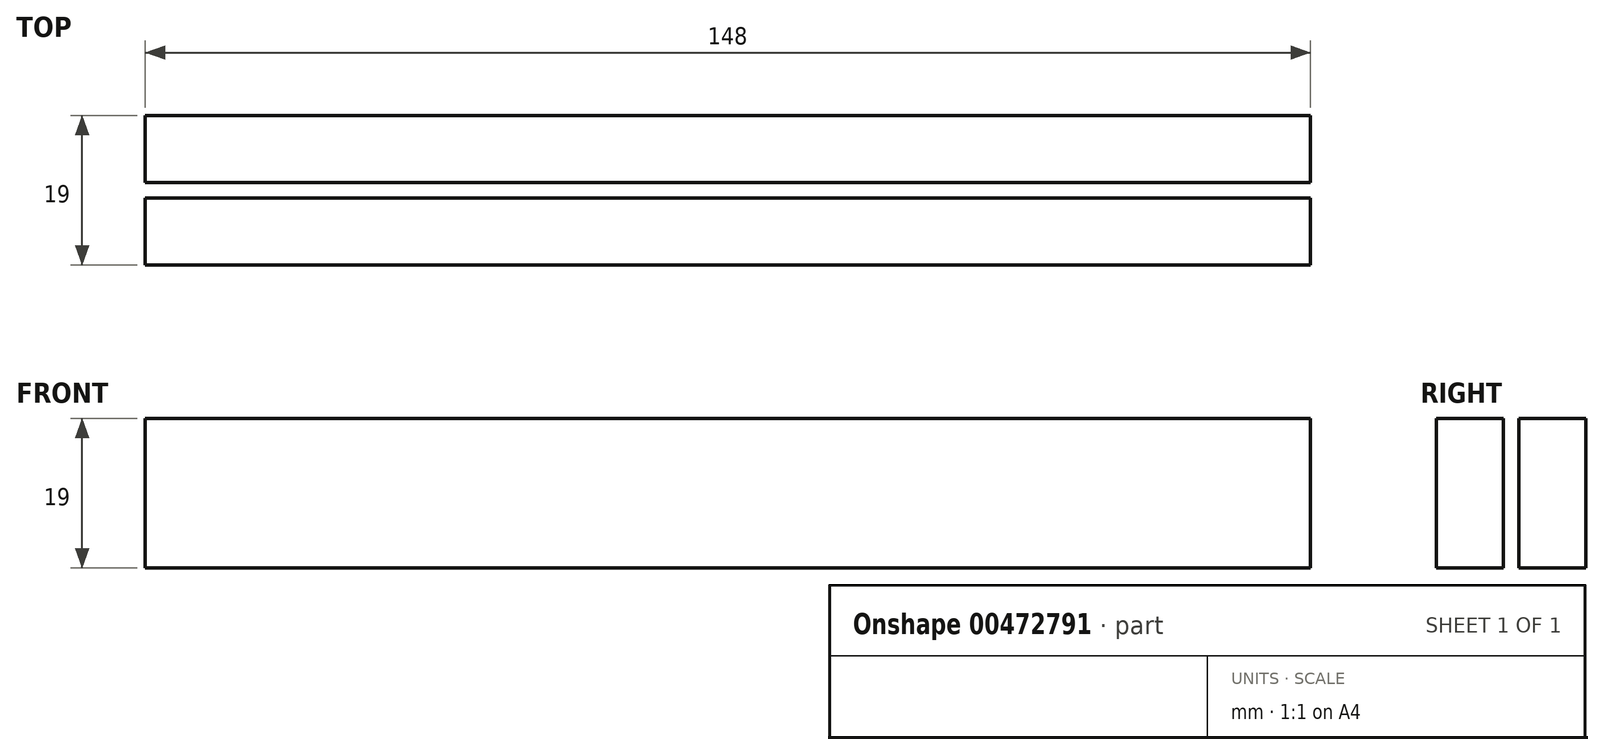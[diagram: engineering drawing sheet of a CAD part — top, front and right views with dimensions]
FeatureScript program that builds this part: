
annotation { "Feature Type Name" : "Feature", "Feature Type Description" : "" }
export const myFeature = defineFeature(function(context is Context, id is Id, definition is map)
    precondition{}
    {
        {
            var Q0;
            Q0=qCreatedBy(makeId("Top.planeOp"),FACE);
            var sketch = newSketch(context, id + "F0", { "sketchPlane" : qUnion([Q0])});
            skLineSegment(sketch, "E0.bottom", {"start": v(74, -9.5) * mm, "end": v(-74, -9.5) * mm});
            skLineSegment(sketch, "E0.top", {"start": v(74, 9.5) * mm, "end": v(-74, 9.5) * mm});
            skLineSegment(sketch, "E0.left", {"start": v(74, -9.5) * mm, "end": v(74, 9.5) * mm});
            skLineSegment(sketch, "E0.right", {"start": v(-74, -9.5) * mm, "end": v(-74, 9.5) * mm});
            skPoint(sketch, "E0.middle", {"position": v(0, 0) * mm});
            skSolve(sketch);
        }
        {
            var Q0;
            Q0=makeQuery(id+"F0.imprint","IMPRINT",FACE,{"disambiguationData":[TD([[makeQuery(id+"F0.imprint","IMPRINT",EDGE,{"derivedFrom":sQuery(id+"F0.wireOp",EDGE,"E0.bottom")}),-1.0]])]});
            extrude(context, id + "F1", {"entities" : qUnion([Q0]), "depth" : 19 * mm});
        }
        {
            var Q0;
            Q0=makeQuery(id+"F1.opExtrude","CAP_FACE",FACE,{"disambiguationData":[OSD([sQuery(id+"F0.wireOp",EDGE,"E0.bottom"),sQuery(id+"F0.wireOp",EDGE,"E0.top"),sQuery(id+"F0.wireOp",EDGE,"E0.left"),sQuery(id+"F0.wireOp",EDGE,"E0.right")])],"isStart":false});
            var sketch = newSketch(context, id + "F2", { "sketchPlane" : qUnion([Q0])});
            skLineSegment(sketch, "E1", {"start": v(-74, 9.5) * mm, "end": v(-74, -9.5) * mm, "construction": true});
            skLineSegment(sketch, "E2", {"start": v(-74, 0) * mm, "end": v(-74, 1) * mm, "construction": true});
            skLineSegment(sketch, "E3.bottom", {"start": v(-74, 1) * mm, "end": v(74, 1) * mm});
            skLineSegment(sketch, "E3.top", {"start": v(-74, -1) * mm, "end": v(74, -1) * mm});
            skLineSegment(sketch, "E3.left", {"start": v(-74, 1) * mm, "end": v(-74, -1) * mm});
            skLineSegment(sketch, "E3.right", {"start": v(74, 1) * mm, "end": v(74, -1) * mm});
            skSolve(sketch);
        }
        {
            var Q0;
            Q0=makeQuery(id+"F2.imprint","IMPRINT",FACE,{"disambiguationData":[TD([[makeQuery(id+"F2.imprint","IMPRINT",EDGE,{"derivedFrom":sQuery(id+"F2.wireOp",EDGE,"E3.bottom")}),-1.0]])]});
            extrude(context, id + "F3", {"entities" : qUnion([Q0]), "operationType" : NewBodyOperationType.REMOVE, "endBound" : BoundingType.UP_TO_NEXT, "oppositeDirection" : true, "depth" : 25 * mm});
        }
    });
